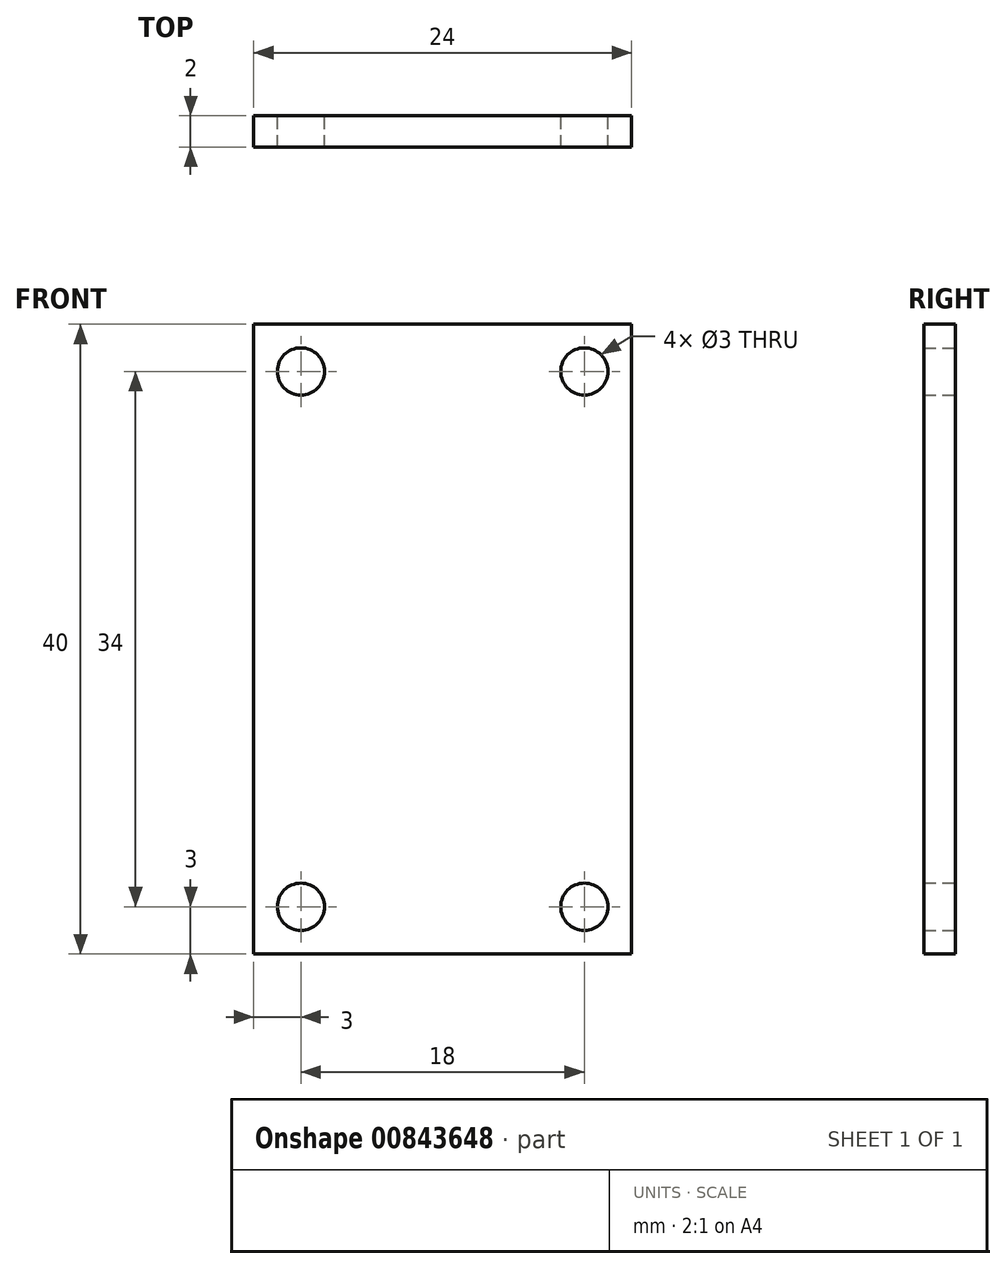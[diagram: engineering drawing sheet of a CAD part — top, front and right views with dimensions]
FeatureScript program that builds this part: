
annotation { "Feature Type Name" : "Feature", "Feature Type Description" : "" }
export const myFeature = defineFeature(function(context is Context, id is Id, definition is map)
    precondition{}
    {
        {
            var Q0;
            Q0=qCreatedBy(makeId("Front.planeOp"),FACE);
            var sketch = newSketch(context, id + "F0", { "sketchPlane" : qUnion([Q0])});
            skLineSegment(sketch, "E0.bottom", {"start": v(12, -20) * mm, "end": v(-12, -20) * mm});
            skLineSegment(sketch, "E0.top", {"start": v(12, 20) * mm, "end": v(-12, 20) * mm});
            skLineSegment(sketch, "E0.left", {"start": v(12, -20) * mm, "end": v(12, 20) * mm});
            skLineSegment(sketch, "E0.right", {"start": v(-12, -20) * mm, "end": v(-12, 20) * mm});
            skPoint(sketch, "E0.middle", {"position": v(0, 0) * mm});
            skCircle(sketch, "E1", {"center": v(-9, 17) * mm, "radius": 1.5 * mm});
            skCircle(sketch, "E2.MirrorC", {"center": v(9, 17) * mm, "radius": 1.5 * mm});
            skCircle(sketch, "E3.MirrorC", {"center": v(9, -17) * mm, "radius": 1.5 * mm});
            skCircle(sketch, "E4.MirrorC", {"center": v(-9, -17) * mm, "radius": 1.5 * mm});
            skSolve(sketch);
        }
        {
            var Q0;
            Q0=makeQuery(id+"F0.imprint","IMPRINT",FACE,{"disambiguationData":[TD([[makeQuery(id+"F0.imprint","IMPRINT",EDGE,{"derivedFrom":sQuery(id+"F0.wireOp",EDGE,"E0.bottom")}),-1.0]])]});
            extrude(context, id + "F1", {"entities" : qUnion([Q0]), "depth" : 2 * mm, "offsetDistance" : 25 * mm});
        }
    });
